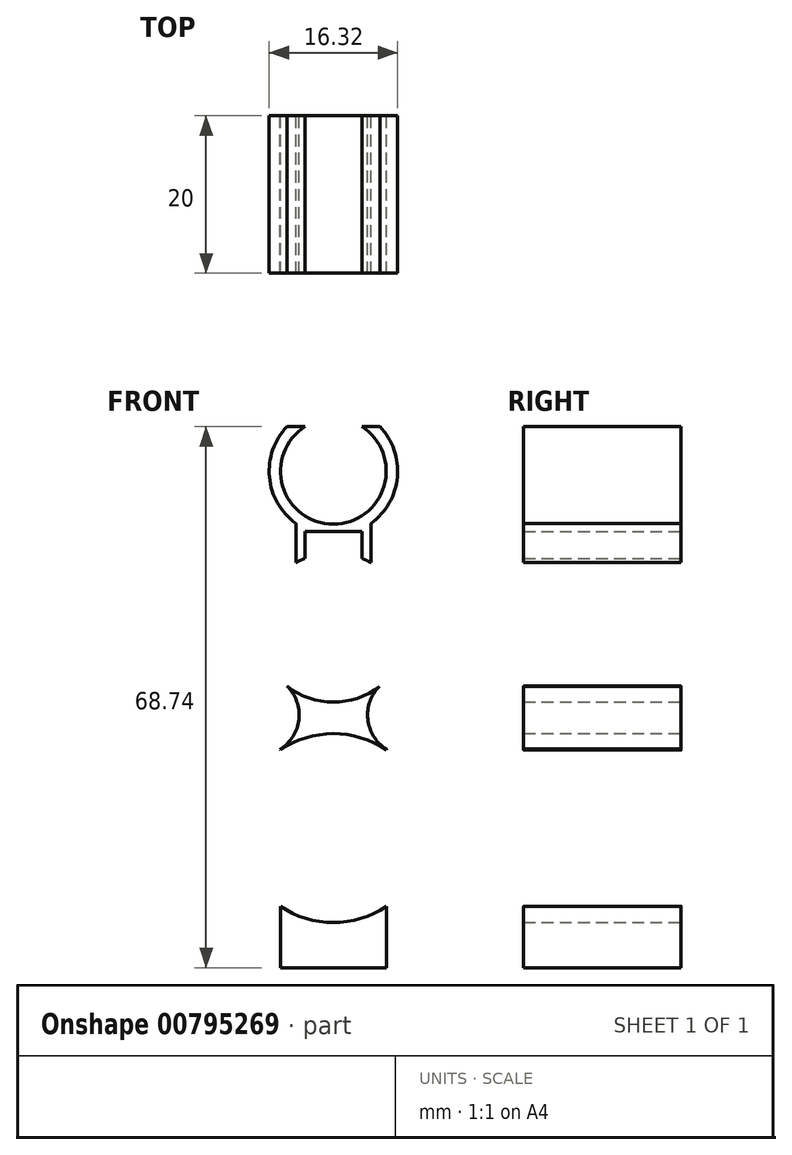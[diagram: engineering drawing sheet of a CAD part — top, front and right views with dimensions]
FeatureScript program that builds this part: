
annotation { "Feature Type Name" : "Feature", "Feature Type Description" : "" }
export const myFeature = defineFeature(function(context is Context, id is Id, definition is map)
    precondition{}
    {
        {
            var Q0;
            Q0=qCreatedBy(makeId("Front.planeOp"),FACE);
            var sketch = newSketch(context, id + "F0", { "sketchPlane" : qUnion([Q0])});
            skCircle(sketch, "E0", {"center": v(0, 0) * mm, "radius": 7.5 * mm});
            skCircle(sketch, "E1", {"center": v(0, 0) * mm, "radius": 8.5 * mm});
            skCircle(sketch, "E2", {"center": v(0, -25.5) * mm, "radius": 11 * mm});
            skCircle(sketch, "E3", {"center": v(0, 0) * mm, "radius": 9.5 * mm});
            skCircle(sketch, "E4", {"center": v(0, -25.5) * mm, "radius": 12 * mm});
            skLineSegment(sketch, "E5", {"start": v(-9.5, 0.03) * mm, "end": v(-9.5, -0.03) * mm});
            skLineSegment(sketch, "E6", {"start": v(9.5, 0.1) * mm, "end": v(9.5, -0.1) * mm});
            skArc(sketch, "E7", {"start": v(-6.8, -15.5) * mm, "mid": v(-4.36, -11.35) * mm, "end": v(-6.42, -7) * mm});
            skArc(sketch, "E8", {"start": v(6.46, -6.97) * mm, "mid": v(4.35, -11.28) * mm, "end": v(6.72, -15.46) * mm});
            skPoint(sketch, "E9", {"position": v(-6.74, -15.57) * mm});
            skPoint(sketch, "E10", {"position": v(-6.8, -15.5) * mm});
            skPoint(sketch, "E11", {"position": v(6.72, -15.46) * mm});
            skLineSegment(sketch, "E12", {"start": v(6.72, -15.46) * mm, "end": v(6.72, -15.56) * mm});
            skLineSegment(sketch, "E13", {"start": v(-6.8, -15.5) * mm, "end": v(-6.74, -15.57) * mm});
            skLineSegment(sketch, "E14", {"start": v(6.72, -15.46) * mm, "end": v(6.72, -16.79) * mm});
            skLineSegment(sketch, "E15", {"start": v(-6.74, -43.24) * mm, "end": v(6.72, -43.24) * mm});
            skArc(sketch, "E16", {"start": v(-3.62, 25.5) * mm, "mid": v(-6.45, 17.95) * mm, "end": v(0, 13.13) * mm});
            skLineSegment(sketch, "E17", {"start": v(-4.77, 13.21) * mm, "end": v(-4.77, 8.22) * mm});
            skLineSegment(sketch, "E18", {"start": v(-3.62, 12.18) * mm, "end": v(0, 12.18) * mm});
            skLineSegment(sketch, "E19", {"start": v(-3.62, 12.18) * mm, "end": v(-3.62, 8.78) * mm});
            skLineSegment(sketch, "E20", {"start": v(-5.89, 25.5) * mm, "end": v(-3.62, 25.5) * mm});
            skArc(sketch, "E21.trimOffspring", {"start": v(-5.89, 25.5) * mm, "mid": v(-8.13, 19.1) * mm, "end": v(-4.77, 13.21) * mm});
            skPoint(sketch, "E22.end.orphan", {"position": v(5.23, 7.93) * mm});
            skPoint(sketch, "E23.MirrorCS.end.orphan", {"position": v(-5.91, 8.78) * mm});
            skPoint(sketch, "E23.MirrorCS.start.orphan", {"position": v(-5.91, 12.18) * mm});
            skPoint(sketch, "E24.MirrorCS.end.orphan", {"position": v(-14.77, 7.93) * mm});
            skPoint(sketch, "E24.MirrorCS.start.orphan", {"position": v(-14.77, 13.57) * mm});
            skPoint(sketch, "E25", {"position": v(0, 13.13) * mm});
            skPoint(sketch, "E26", {"position": v(0, 12.18) * mm});
            skPoint(sketch, "E27.start.orphan", {"position": v(3.38, 12.18) * mm});
            skPoint(sketch, "E28.start.orphan", {"position": v(5.23, 13.57) * mm});
            skLineSegment(sketch, "E29", {"start": v(0, 13.13) * mm, "end": v(0, 12.18) * mm});
            skPoint(sketch, "E30.MirrorP", {"position": v(-7.24, 12.18) * mm});
            skArc(sketch, "E31.MirrorCS", {"start": v(3.62, 25.5) * mm, "mid": v(6.45, 17.95) * mm, "end": v(0, 13.13) * mm});
            skLineSegment(sketch, "E32.MirrorCS", {"start": v(5.89, 25.5) * mm, "end": v(3.62, 25.5) * mm});
            skArc(sketch, "E33.MirrorCS", {"start": v(5.89, 25.5) * mm, "mid": v(8.13, 19.1) * mm, "end": v(4.77, 13.21) * mm});
            skLineSegment(sketch, "E34.MirrorCS", {"start": v(3.62, 12.18) * mm, "end": v(0, 12.18) * mm});
            skLineSegment(sketch, "E35.MirrorCS", {"start": v(3.62, 12.18) * mm, "end": v(3.62, 8.78) * mm});
            skLineSegment(sketch, "E36.MirrorCS", {"start": v(4.77, 13.21) * mm, "end": v(4.77, 8.22) * mm});
            skLineSegment(sketch, "E37.trimOffspring", {"start": v(-6.74, -35.43) * mm, "end": v(-6.74, -43.24) * mm});
            skLineSegment(sketch, "E38.trimOffspring", {"start": v(6.72, -35.44) * mm, "end": v(6.72, -43.24) * mm});
            skSolve(sketch);
        }
        {
            var Q0;
            Q0=makeQuery(id+"F0.imprint","IMPRINT",FACE,{"disambiguationData":[TD([[makeQuery(id+"F0.imprint","IMPRINT",EDGE,{"derivedFrom":sQuery(id+"F0.wireOp",EDGE,"E16")}),-1.0]])]});
            var Q1;
            Q1=makeQuery(id+"F0.imprint","IMPRINT",FACE,{"disambiguationData":[TD([[makeQuery(id+"F0.imprint","IMPRINT",EDGE,{"derivedFrom":sQuery(id+"F0.wireOp",EDGE,"E29")}),1.0]])]});
            var Q2;
            Q2=makeQuery(id+"F0.imprint","IMPRINT",FACE,{"disambiguationData":[TD([[makeQuery(id+"F0.imprint","IMPRINT",EDGE,{"derivedFrom":sQuery(id+"F0.wireOp",EDGE,"E15")}),1.0]])]});
            var Q3;
            {var subQ5=sQuery(id+"F0.wireOp",EDGE,"E13");Q3=makeQuery(id+"F0.imprint","IMPRINT",FACE,{"disambiguationData":[TD([[makeQuery(id+"F0.imprint","IMPRINT",EDGE,{"derivedFrom":subQ5}),1.0]])]});}
            extrude(context, id + "F1", {"entities" : qUnion([Q0, Q1, Q2, Q3]), "depth" : 20 * mm, "offsetDistance" : 25 * mm});
        }
    });
